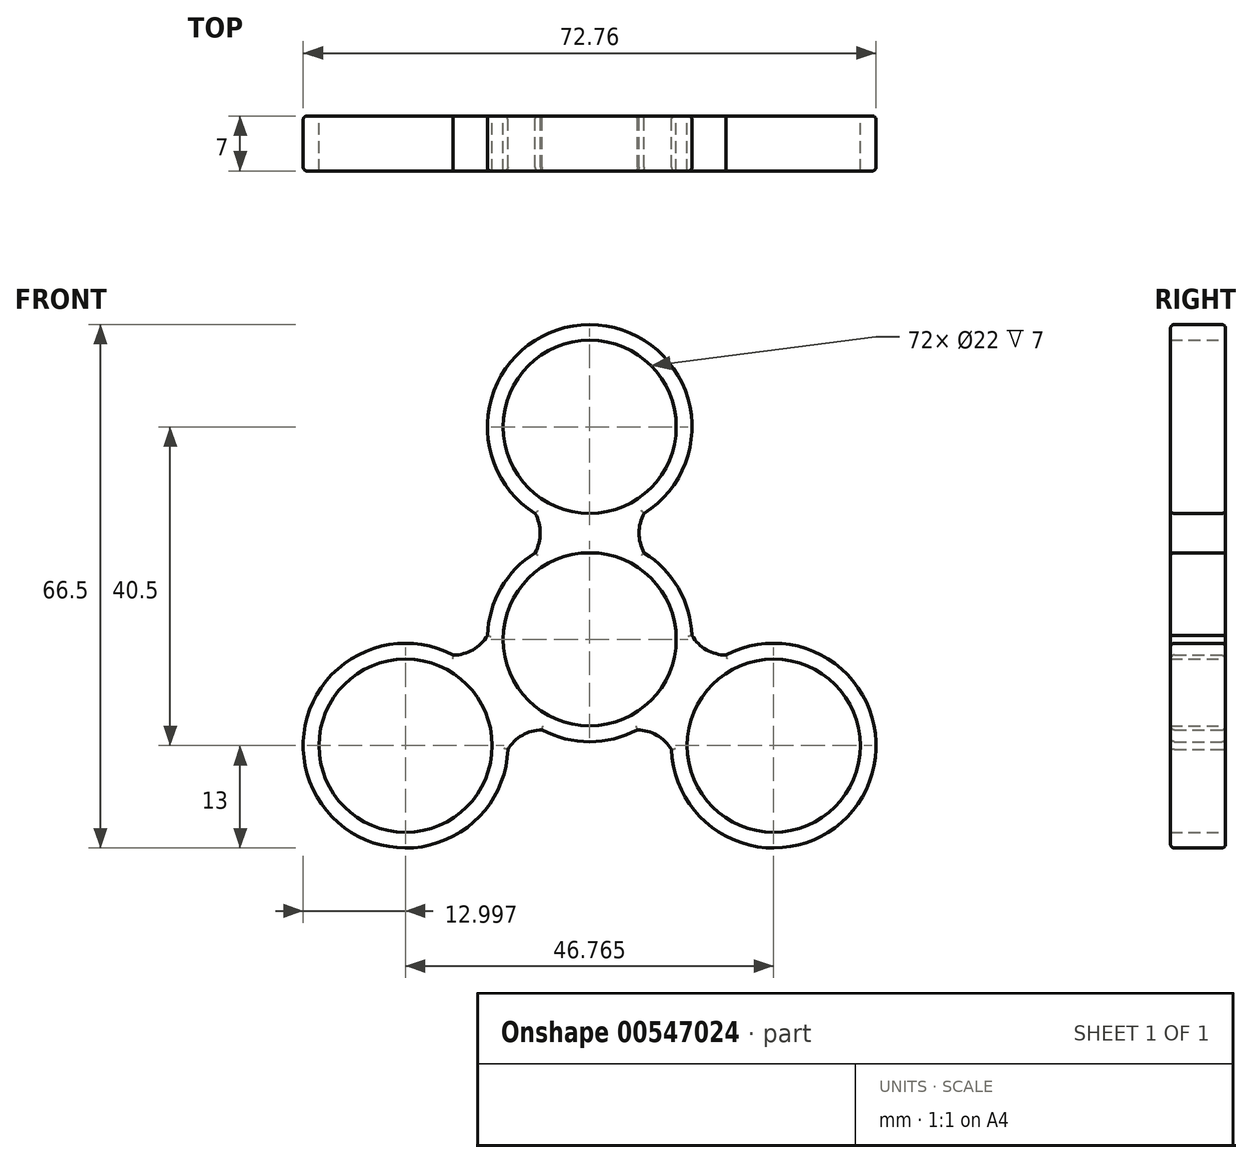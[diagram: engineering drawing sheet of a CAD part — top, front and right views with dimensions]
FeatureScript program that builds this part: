
annotation { "Feature Type Name" : "Feature", "Feature Type Description" : "" }
export const myFeature = defineFeature(function(context is Context, id is Id, definition is map)
    precondition{}
    {
        {
            var Q0;
            Q0=qCreatedBy(makeId("Front.planeOp"),FACE);
            var sketch = newSketch(context, id + "F0", { "sketchPlane" : qUnion([Q0])});
            skCircle(sketch, "E0", {"center": v(0, 0) * mm, "radius": 11 * mm});
            skCircle(sketch, "E1", {"center": v(0, 0) * mm, "radius": 13 * mm});
            skPoint(sketch, "E2", {"position": v(0, 27) * mm});
            skCircle(sketch, "E3", {"center": v(0, 27) * mm, "radius": 11 * mm});
            skCircle(sketch, "E4", {"center": v(0, 27) * mm, "radius": 13 * mm});
            skLineSegment(sketch, "E5", {"start": v(0, 0) * mm, "end": v(23.38, -13.5) * mm});
            skCircle(sketch, "E6", {"center": v(23.38, -13.5) * mm, "radius": 11 * mm});
            skCircle(sketch, "E7", {"center": v(23.38, -13.5) * mm, "radius": 13 * mm});
            skLineSegment(sketch, "E8", {"start": v(0, 0) * mm, "end": v(-23.38, -13.5) * mm});
            skCircle(sketch, "E9", {"center": v(-23.38, -13.5) * mm, "radius": 11 * mm});
            skCircle(sketch, "E10", {"center": v(-23.38, -13.5) * mm, "radius": 13 * mm});
            skPoint(sketch, "E11.middle", {"position": v(0, 13.5) * mm});
            skArc(sketch, "E12", {"start": v(-6.93, 11) * mm, "mid": v(-6.27, 13.5) * mm, "end": v(-6.93, 16) * mm});
            skArc(sketch, "E13", {"start": v(6.93, 16) * mm, "mid": v(6.27, 13.5) * mm, "end": v(6.93, 11) * mm});
            skArc(sketch, "E14", {"start": v(13, 0.5) * mm, "mid": v(14.83, -1.32) * mm, "end": v(17.32, -2) * mm});
            skArc(sketch, "E15", {"start": v(10.4, -14) * mm, "mid": v(8.56, -12.18) * mm, "end": v(6.06, -11.5) * mm});
            skArc(sketch, "E16", {"start": v(-17.32, -2) * mm, "mid": v(-14.83, -1.32) * mm, "end": v(-13, 0.5) * mm});
            skArc(sketch, "E17", {"start": v(-6.06, -11.5) * mm, "mid": v(-8.56, -12.18) * mm, "end": v(-10.4, -14) * mm});
            skSolve(sketch);
        }
        {
            var Q0;
            Q0=qSketchRegion(id+"F0",true);
            extrude(context, id + "F1", {"entities" : qUnion([Q0]), "endBound" : BoundingType.SYMMETRIC, "depth" : 7 * mm, "offsetDistance" : 25.4 * mm});
        }
        {
            var Q0;
            {var subQ0=sQuery(id+"F0.wireOp",EDGE,"E1");Q0=makeQuery(id+"F1.opExtrude","CAP_EDGE",EDGE,{"disambiguationData":[OSD([subQ0]),TDD([makeQuery(id+"F0.imprint","IMPRINT",EDGE,{"disambiguationData":[TD([[makeQuery(id+"F0.imprint","INTERSECT",VERTEX,{"derivedFrom":[subQ0,sQuery(id+"F0.wireOp",EDGE,"E12")]}),-1.0]])],"derivedFrom":subQ0})])],"isStart":true});}
            var Q1;
            Q1=makeQuery(id+"F1.opExtrude","CAP_EDGE",EDGE,{"disambiguationData":[OSD([sQuery(id+"F0.wireOp",EDGE,"E4")])],"isStart":false});
            var Q2;
            Q2=makeQuery(id+"F1.opExtrude","CAP_EDGE",EDGE,{"disambiguationData":[OSD([sQuery(id+"F0.wireOp",EDGE,"E4")])],"isStart":true});
            var Q3;
            {var subQ0=sQuery(id+"F0.wireOp",EDGE,"E1");Q3=makeQuery(id+"F1.opExtrude","CAP_EDGE",EDGE,{"disambiguationData":[OSD([subQ0]),TDD([makeQuery(id+"F0.imprint","IMPRINT",EDGE,{"disambiguationData":[TD([[makeQuery(id+"F0.imprint","INTERSECT",VERTEX,{"derivedFrom":[subQ0,sQuery(id+"F0.wireOp",EDGE,"E13")]}),1.0]])],"derivedFrom":subQ0})])],"isStart":false});}
            var Q4;
            {var subQ0=sQuery(id+"F0.wireOp",EDGE,"E1");Q4=makeQuery(id+"F1.opExtrude","CAP_EDGE",EDGE,{"disambiguationData":[OSD([subQ0]),TDD([makeQuery(id+"F0.imprint","IMPRINT",EDGE,{"disambiguationData":[TD([[makeQuery(id+"F0.imprint","INTERSECT",VERTEX,{"derivedFrom":[subQ0,sQuery(id+"F0.wireOp",EDGE,"E12")]}),-1.0]])],"derivedFrom":subQ0})])],"isStart":false});}
            var Q5;
            {var subQ0=sQuery(id+"F0.wireOp",EDGE,"E1");Q5=makeQuery(id+"F1.opExtrude","CAP_EDGE",EDGE,{"disambiguationData":[OSD([subQ0]),TDD([makeQuery(id+"F0.imprint","IMPRINT",EDGE,{"disambiguationData":[TD([[makeQuery(id+"F0.imprint","INTERSECT",VERTEX,{"derivedFrom":[subQ0,sQuery(id+"F0.wireOp",EDGE,"E15")]}),1.0]])],"derivedFrom":subQ0})])],"isStart":false});}
            var Q6;
            Q6=makeQuery(id+"F1.opExtrude","CAP_EDGE",EDGE,{"disambiguationData":[OSD([sQuery(id+"F0.wireOp",EDGE,"E10")])],"isStart":true});
            var Q7;
            Q7=makeQuery(id+"F1.opExtrude","CAP_EDGE",EDGE,{"disambiguationData":[OSD([sQuery(id+"F0.wireOp",EDGE,"E10")])],"isStart":false});
            var Q8;
            Q8=makeQuery(id+"F1.opExtrude","CAP_EDGE",EDGE,{"disambiguationData":[OSD([sQuery(id+"F0.wireOp",EDGE,"E7")])],"isStart":false});
            var Q9;
            Q9=makeQuery(id+"F1.opExtrude","CAP_EDGE",EDGE,{"disambiguationData":[OSD([sQuery(id+"F0.wireOp",EDGE,"E7")])],"isStart":true});
            var Q10;
            {var subQ0=sQuery(id+"F0.wireOp",EDGE,"E1");Q10=makeQuery(id+"F1.opExtrude","CAP_EDGE",EDGE,{"disambiguationData":[OSD([subQ0]),TDD([makeQuery(id+"F0.imprint","IMPRINT",EDGE,{"disambiguationData":[TD([[makeQuery(id+"F0.imprint","INTERSECT",VERTEX,{"derivedFrom":[subQ0,sQuery(id+"F0.wireOp",EDGE,"E13")]}),1.0]])],"derivedFrom":subQ0})])],"isStart":true});}
            var Q11;
            Q11=makeQuery(id+"F1.opExtrude","CAP_EDGE",EDGE,{"disambiguationData":[OSD([sQuery(id+"F0.wireOp",EDGE,"E14")])],"isStart":true});
            var Q12;
            Q12=makeQuery(id+"F1.opExtrude","CAP_EDGE",EDGE,{"disambiguationData":[OSD([sQuery(id+"F0.wireOp",EDGE,"E13")])],"isStart":true});
            var Q13;
            Q13=makeQuery(id+"F1.opExtrude","CAP_EDGE",EDGE,{"disambiguationData":[OSD([sQuery(id+"F0.wireOp",EDGE,"E12")])],"isStart":true});
            var Q14;
            Q14=makeQuery(id+"F1.opExtrude","CAP_EDGE",EDGE,{"disambiguationData":[OSD([sQuery(id+"F0.wireOp",EDGE,"E16")])],"isStart":true});
            var Q15;
            Q15=makeQuery(id+"F1.opExtrude","CAP_EDGE",EDGE,{"disambiguationData":[OSD([sQuery(id+"F0.wireOp",EDGE,"E17")])],"isStart":true});
            var Q16;
            {var subQ0=sQuery(id+"F0.wireOp",EDGE,"E1");Q16=makeQuery(id+"F1.opExtrude","CAP_EDGE",EDGE,{"disambiguationData":[OSD([subQ0]),TDD([makeQuery(id+"F0.imprint","IMPRINT",EDGE,{"disambiguationData":[TD([[makeQuery(id+"F0.imprint","INTERSECT",VERTEX,{"derivedFrom":[subQ0,sQuery(id+"F0.wireOp",EDGE,"E15")]}),1.0]])],"derivedFrom":subQ0})])],"isStart":true});}
            var Q17;
            Q17=makeQuery(id+"F1.opExtrude","CAP_EDGE",EDGE,{"disambiguationData":[OSD([sQuery(id+"F0.wireOp",EDGE,"E15")])],"isStart":true});
            var Q18;
            Q18=makeQuery(id+"F1.opExtrude","CAP_EDGE",EDGE,{"disambiguationData":[OSD([sQuery(id+"F0.wireOp",EDGE,"E15")])],"isStart":false});
            var Q19;
            Q19=makeQuery(id+"F1.opExtrude","CAP_EDGE",EDGE,{"disambiguationData":[OSD([sQuery(id+"F0.wireOp",EDGE,"E17")])],"isStart":false});
            var Q20;
            Q20=makeQuery(id+"F1.opExtrude","CAP_EDGE",EDGE,{"disambiguationData":[OSD([sQuery(id+"F0.wireOp",EDGE,"E16")])],"isStart":false});
            var Q21;
            Q21=makeQuery(id+"F1.opExtrude","CAP_EDGE",EDGE,{"disambiguationData":[OSD([sQuery(id+"F0.wireOp",EDGE,"E12")])],"isStart":false});
            var Q22;
            Q22=makeQuery(id+"F1.opExtrude","CAP_EDGE",EDGE,{"disambiguationData":[OSD([sQuery(id+"F0.wireOp",EDGE,"E14")])],"isStart":false});
            var Q23;
            Q23=makeQuery(id+"F1.opExtrude","CAP_EDGE",EDGE,{"disambiguationData":[OSD([sQuery(id+"F0.wireOp",EDGE,"E13")])],"isStart":false});
            fillet(context, id + "F2", {"entities" : qUnion([Q0, Q1, Q2, Q3, Q4, Q5, Q6, Q7, Q8, Q9, Q10, Q11, Q12, Q13, Q14, Q15, Q16, Q17, Q18, Q19, Q20, Q21, Q22, Q23]), "radius" : 0.5 * mm, "tangentPropagation" : true, "allowEdgeOverflow" : false});
        }
    });
